# Revit family: Sanitary_Hand-Hair-Dryers_JVD_JVD-SUP-AIR-HAND-DRYERS_
name_source: partatom
category: Specialty Equipment
units: mm (PartAtom-declared; Revit-internal decimal feet)

## family parameters
Cut with Voids When Loaded = No
Host = Face
OmniClass Number = 23.31.25.15
OmniClass Title = Hand Dryers
Part Type = Normal
Room Calculation Point = No
Round Connector Dimension = Use Diameter
Shared = No

## types (7) — shared parameters
Air outlet temperature (°C) = 40
Apparent Load = 600 VA
Connector Description = Electrical Connection. Exist in 110-120 V (US)
Current = 1 A
Depth = 193 mm  [stored 0.633202 ft]
Description = SUP'AIR hand dryer with ultra fast drying and low power consumption. Designed for intensive use.
Detection type = Infrared
Drying time (s) = 10-15s
Drying zone lighting = Yes
Frequency (Hz) = 50
Height = 292 mm  [stored 0.958005 ft]
Manufacturer = JVD
Material = ABS
Model = SUP’AIR
Motor lifetime (number of operations) = 350000
Motor speed (rpm) = 24000
Number of Poles = 1
Outlet air speed (m/s) = 90
Power Factor = 1
Product data url = https://bimobject.com
Safety in case of malfunction = Yes
Sound level (dB) (1m in front of the appliance) = 75
Standby power consumption (W) = 2.2000
Type of motor = Brushed AC
URL = www.jvd.fr/en/
Vandal-safe = Yes
Voltage = 230 V
Weight = 3.42 kg
Width = 215 mm
zero-valued in all types: Default Elevation, Edition number, Version

## per-type parameters (varying)
| type | Colour | Filter | z_Base Variation | z_Kids Variation |
| 8111056 SUP’AIR White | JVD - Plastic - White - RAL 9016 | Anti-bacterial filter (Option) | Yes | No |
| 8111056KIDs SUP'AIR Kids White | JVD - Plastic - Kids White | Anti-bacterial filter (Option) | No | Yes |
| 8111057 SUP'AIR Metallic Gray | JVD - Plastic - Metallic Gray - RAL 9006 | Anti-bacterial filter (Option) | Yes | No |
| 8112159 SUP'AIR Fresh White | JVD - Plastic - Fresh White - RAL 9016 | No | Yes | No |
| 8111760 SUP'AIR Matte Black | JVD - Plastic - Matte Black - RAL 9005 | Anti-bacterial filter (Option) | Yes | No |
| 8112177 SUP'AIR Fresh Metallic Gray | JVD - Plastic - Fresh Metallic Gray - RAL 9006 | No | Yes | No |
| 8112178 SUP'AIR Fresh Matte Black | JVD - Plastic - Fresh Matte Black - RAL 9005 | No | Yes | No |

note: [stored X ft] marks values corroborated as IEEE doubles in the binary element streams (Revit-internal decimal feet)

## geometry (parser evidence)
native form markers: Sweep x2
no freeform markers — native parametric forms only
